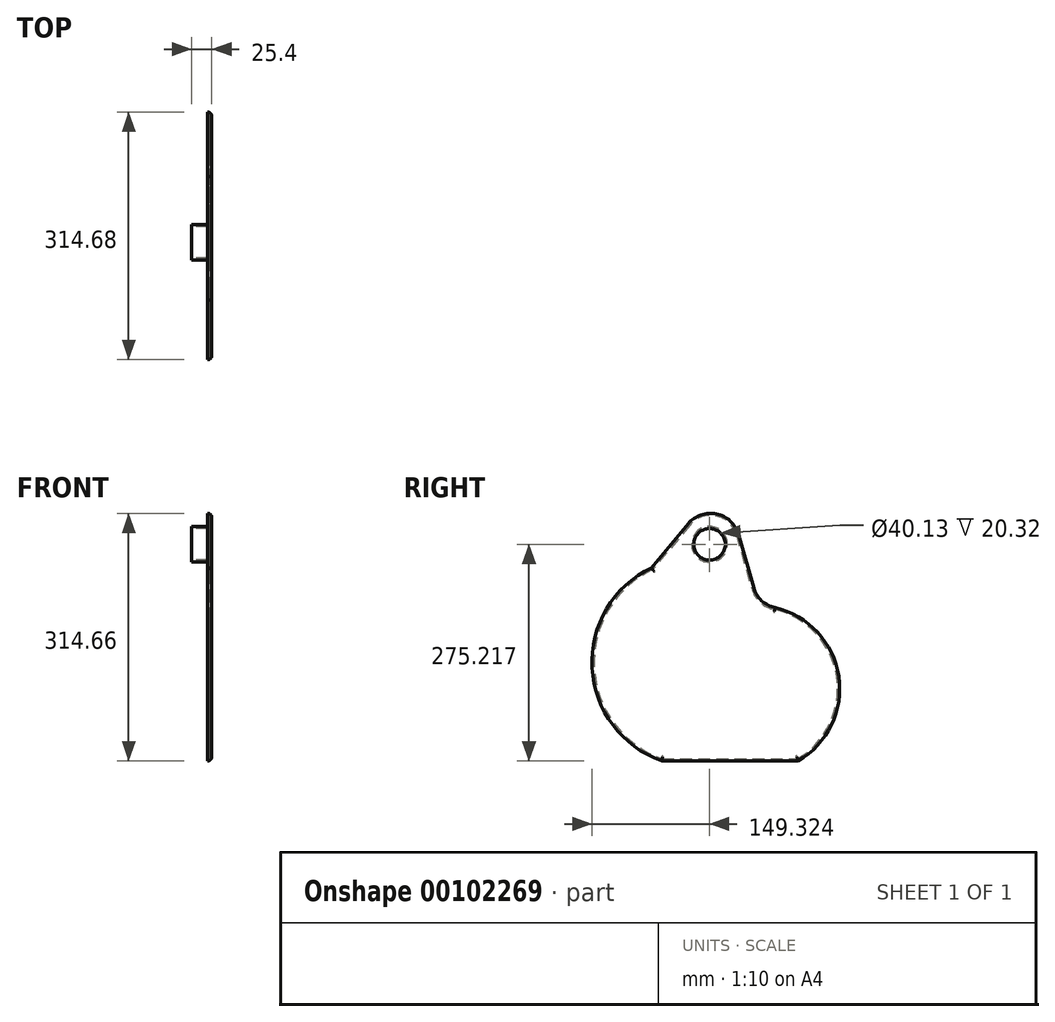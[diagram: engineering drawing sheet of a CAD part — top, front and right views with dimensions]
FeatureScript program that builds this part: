
annotation { "Feature Type Name" : "Feature", "Feature Type Description" : "" }
export const myFeature = defineFeature(function(context is Context, id is Id, definition is map)
    precondition{}
    {
        {
            var Q0;
            Q0=qCreatedBy(makeId("Right.planeOp"),FACE);
            var sketch = newSketch(context, id + "F0", { "sketchPlane" : qUnion([Q0])});
            skLineSegment(sketch, "E0", {"start": v(-65.89, -93.64) * mm, "end": v(-65.89, -189.1) * mm, "construction": true});
            skLineSegment(sketch, "E1", {"start": v(92.86, -98.66) * mm, "end": v(92.86, -191.56) * mm, "construction": true});
            skCircle(sketch, "E2", {"center": v(11.15, 199.22) * mm, "radius": 20.06 * mm});
            skArc(sketch, "E3", {"start": v(-62.74, 169.24) * mm, "mid": v(-137.98, 42.2) * mm, "end": v(-49.48, -76) * mm});
            skPoint(sketch, "E3.first.point", {"position": v(-97.47, 145.12) * mm});
            skPoint(sketch, "E3.second.point", {"position": v(-135.65, 23.58) * mm});
            skPoint(sketch, "E3.third.point", {"position": v(-49.48, -76) * mm});
            skArc(sketch, "E4", {"start": v(123.67, -76) * mm, "mid": v(175.2, 32.25) * mm, "end": v(92.7, 119.25) * mm});
            skPoint(sketch, "E4.first.point", {"position": v(123.67, -76) * mm});
            skPoint(sketch, "E4.second.point", {"position": v(176.5, 15.86) * mm});
            skPoint(sketch, "E4.third.point", {"position": v(120.01, 109.35) * mm});
            skArc(sketch, "E5", {"start": v(67.43, 143.62) * mm, "mid": v(77.45, 127.44) * mm, "end": v(94.44, 118.86) * mm});
            skPoint(sketch, "E5.first.point", {"position": v(67.99, 141.86) * mm});
            skPoint(sketch, "E5.second.point", {"position": v(78.15, 126.82) * mm});
            skPoint(sketch, "E5.third.point", {"position": v(94.44, 118.86) * mm});
            skArc(sketch, "E6", {"start": v(47.69, 212.14) * mm, "mid": v(20.02, 237.87) * mm, "end": v(-15.68, 225.51) * mm});
            skPoint(sketch, "E6.first.point", {"position": v(47.98, 211.06) * mm});
            skPoint(sketch, "E6.second.point", {"position": v(25.95, 236.08) * mm});
            skPoint(sketch, "E6.third.point", {"position": v(-13.96, 227.43) * mm});
            skLineSegment(sketch, "E7", {"start": v(47.69, 212.14) * mm, "end": v(67.43, 143.62) * mm});
            skLineSegment(sketch, "E8", {"start": v(-15.68, 225.51) * mm, "end": v(-62.74, 169.24) * mm});
            skLineSegment(sketch, "E9", {"start": v(-49.48, -76) * mm, "end": v(123.67, -76) * mm});
            skSolve(sketch);
        }
        {
            var Q0;
            Q0=makeQuery(id+"F0.imprint","IMPRINT",FACE,{"disambiguationData":[TD([[makeQuery(id+"F0.imprint","IMPRINT",EDGE,{"derivedFrom":sQuery(id+"F0.wireOp",EDGE,"E2")}),-1.0]])]});
            extrude(context, id + "F1", {"entities" : qUnion([Q0]), "depth" : 25.4 * mm});
        }
        {
            var Q0;
            Q0=makeQuery(id+"F1.opExtrude","CAP_FACE",FACE,{"disambiguationData":[OSD([sQuery(id+"F0.wireOp",EDGE,"E2"),sQuery(id+"F0.wireOp",EDGE,"E3"),sQuery(id+"F0.wireOp",EDGE,"E4"),sQuery(id+"F0.wireOp",EDGE,"E5"),sQuery(id+"F0.wireOp",EDGE,"E6"),sQuery(id+"F0.wireOp",EDGE,"E7"),sQuery(id+"F0.wireOp",EDGE,"E8"),sQuery(id+"F0.wireOp",EDGE,"E9")])],"isStart":true});
            shell(context, id + "F2", {"entities" : qUnion([Q0]), "thickness" : 2.54 * mm});
        }
        {
            var Q0;
            {var subQ0=sQuery(id+"F0.wireOp",EDGE,"E9");var subQ1=sQuery(id+"F0.wireOp",EDGE,"E8");var subQ2=sQuery(id+"F0.wireOp",EDGE,"E7");var subQ3=sQuery(id+"F0.wireOp",EDGE,"E6");var subQ4=sQuery(id+"F0.wireOp",EDGE,"E5");var subQ5=sQuery(id+"F0.wireOp",EDGE,"E4");var subQ6=sQuery(id+"F0.wireOp",EDGE,"E3");var subQ7=sQuery(id+"F0.wireOp",EDGE,"E2");Q0=makeQuery(id+"F2.opShell","OFFSET_FACE",FACE,{"disambiguationData":[OSD([subQ7,subQ6,subQ5,subQ4,subQ3,subQ2,subQ1,subQ0]),TDD([makeQuery(id+"F1.opExtrude","CAP_FACE",FACE,{"disambiguationData":[OSD([subQ7,subQ6,subQ5,subQ4,subQ3,subQ2,subQ1,subQ0])],"isStart":true})])]});}
            extrude(context, id + "F3", {"entities" : qUnion([Q0]), "operationType" : NewBodyOperationType.REMOVE, "oppositeDirection" : true, "depth" : 20.32 * mm});
        }
        {
            var Q0;
            Q0=makeQuery(id+"F1.opExtrude","CAP_FACE",FACE,{"disambiguationData":[OSD([sQuery(id+"F0.wireOp",EDGE,"E2"),sQuery(id+"F0.wireOp",EDGE,"E3"),sQuery(id+"F0.wireOp",EDGE,"E4"),sQuery(id+"F0.wireOp",EDGE,"E5"),sQuery(id+"F0.wireOp",EDGE,"E6"),sQuery(id+"F0.wireOp",EDGE,"E7"),sQuery(id+"F0.wireOp",EDGE,"E8"),sQuery(id+"F0.wireOp",EDGE,"E9")])],"isStart":false});
            fillet(context, id + "F4", {"entities" : qUnion([Q0]), "radius" : 5.08 * mm, "tangentPropagation" : true, "allowEdgeOverflow" : false});
        }
        {
            var Q0;
            {var subQ0=sQuery(id+"F0.wireOp",EDGE,"E9");var subQ1=sQuery(id+"F0.wireOp",EDGE,"E8");var subQ2=sQuery(id+"F0.wireOp",EDGE,"E7");var subQ3=sQuery(id+"F0.wireOp",EDGE,"E6");var subQ4=sQuery(id+"F0.wireOp",EDGE,"E5");var subQ5=sQuery(id+"F0.wireOp",EDGE,"E4");var subQ6=sQuery(id+"F0.wireOp",EDGE,"E3");var subQ7=sQuery(id+"F0.wireOp",EDGE,"E2");Q0=makeQuery(id+"F2.opShell","OFFSET_FACE",FACE,{"disambiguationData":[OSD([subQ7,subQ6,subQ5,subQ4,subQ3,subQ2,subQ1,subQ0]),TDD([makeQuery(id+"F1.opExtrude","CAP_FACE",FACE,{"disambiguationData":[OSD([subQ7,subQ6,subQ5,subQ4,subQ3,subQ2,subQ1,subQ0])],"isStart":false})])]});}
            fillet(context, id + "F5", {"entities" : qUnion([Q0]), "radius" : 5.08 * mm, "allowEdgeOverflow" : false});
        }
    });
